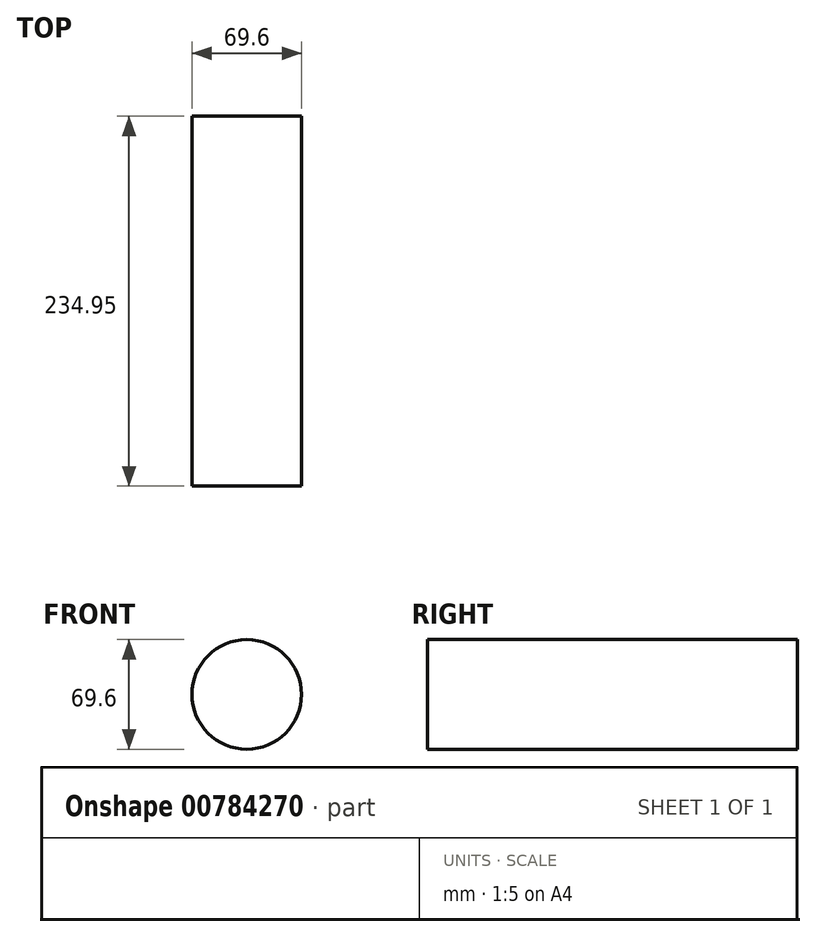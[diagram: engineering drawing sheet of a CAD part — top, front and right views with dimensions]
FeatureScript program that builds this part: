
annotation { "Feature Type Name" : "Feature", "Feature Type Description" : "" }
export const myFeature = defineFeature(function(context is Context, id is Id, definition is map)
    precondition{}
    {
        {
            var Q0;
            Q0=qCreatedBy(makeId("Front.planeOp"),FACE);
            var sketch = newSketch(context, id + "F0", { "sketchPlane" : qUnion([Q0])});
            skCircle(sketch, "E0", {"center": v(0, 0) * mm, "radius": 34.8 * mm});
            skSolve(sketch);
        }
        {
            var Q0;
            Q0 = qSketchRegion(id + "F0", true);
            extrude(context, id + "F1", {"entities" : qUnion([Q0]), "depth" : 6.35 * mm, "offsetDistance" : 25.4 * mm});
        }
        {
            var Q0;
            Q0=makeQuery(id+"F1.opExtrude","CAP_FACE",FACE,{"disambiguationData":[OSD([sQuery(id+"F0.wireOp",EDGE,"E0")])],"isStart":false});
            extrude(context, id + "F2", {"entities" : qUnion([Q0]), "operationType" : NewBodyOperationType.ADD, "depth" : 25.4 * mm, "offsetDistance" : 25.4 * mm});
        }
        {
            var Q0;
            Q0=makeQuery(id+"F2.opExtrude","CAP_FACE",FACE,{"disambiguationData":[OSD([sQuery(id+"F0.wireOp",EDGE,"E0")])],"isStart":false});
            extrude(context, id + "F3", {"entities" : qUnion([Q0]), "operationType" : NewBodyOperationType.ADD, "depth" : 101.6 * mm, "offsetDistance" : 25.4 * mm});
        }
        {
            var Q0;
            Q0=makeQuery(id+"F1.opExtrude","CAP_FACE",FACE,{"disambiguationData":[OSD([sQuery(id+"F0.wireOp",EDGE,"E0")])],"isStart":true});
            extrude(context, id + "F4", {"entities" : qUnion([Q0]), "operationType" : NewBodyOperationType.ADD, "depth" : 101.6 * mm, "offsetDistance" : 25.4 * mm});
        }
    });
